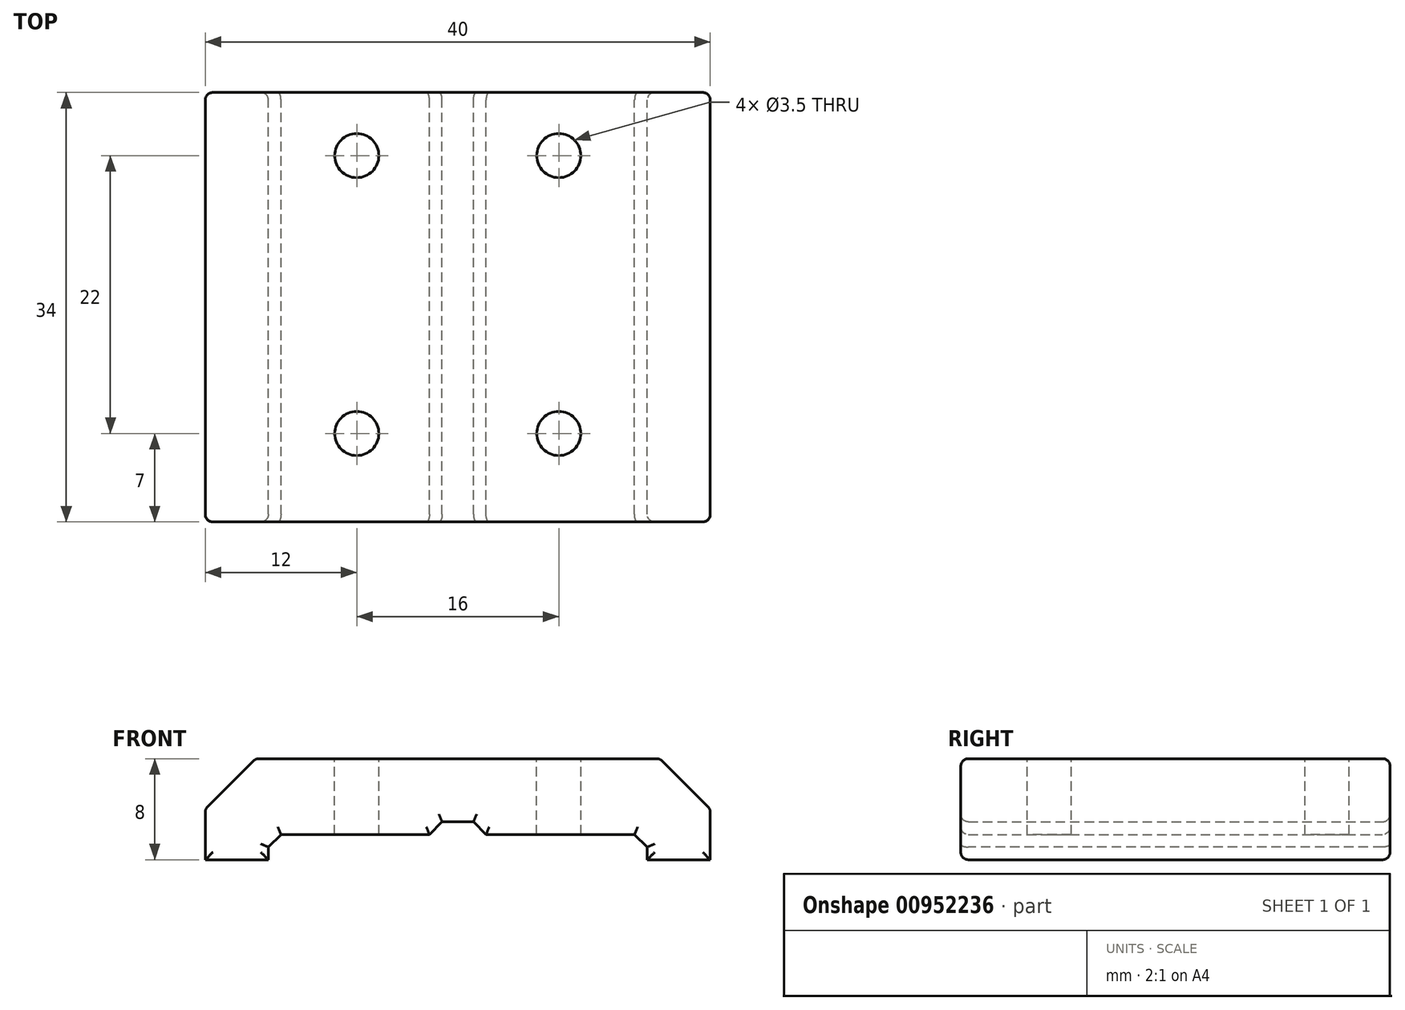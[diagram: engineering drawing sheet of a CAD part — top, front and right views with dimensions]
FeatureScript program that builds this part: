
annotation { "Feature Type Name" : "Feature", "Feature Type Description" : "" }
export const myFeature = defineFeature(function(context is Context, id is Id, definition is map)
    precondition{}
    {
        {
            var Q0;
            Q0=qCreatedBy(makeId("Front.planeOp"),FACE);
            var sketch = newSketch(context, id + "F0", { "sketchPlane" : qUnion([Q0])});
            skLineSegment(sketch, "E0", {"start": v(0, 0) * mm, "end": v(-20, 0) * mm});
            skLineSegment(sketch, "E1", {"start": v(-20, 0) * mm, "end": v(-20, -8) * mm});
            skLineSegment(sketch, "E2", {"start": v(-20, -8) * mm, "end": v(-15, -8) * mm});
            skLineSegment(sketch, "E3", {"start": v(-15, -8) * mm, "end": v(-15, -6) * mm});
            skLineSegment(sketch, "E4", {"start": v(-15, -6) * mm, "end": v(-2.24, -6) * mm});
            skLineSegment(sketch, "E5", {"start": v(-2.24, -6) * mm, "end": v(-1.24, -5) * mm});
            skLineSegment(sketch, "E6", {"start": v(-1.24, -5) * mm, "end": v(0, -5) * mm});
            skLineSegment(sketch, "E7", {"start": v(0, -5) * mm, "end": v(0, 0) * mm});
            skSolve(sketch);
        }
        {
            var Q0;
            Q0 = qSketchRegion(id + "F0", true);
            extrude(context, id + "F1", {"entities" : qUnion([Q0]), "depth" : 34 * mm, "offsetDistance" : 25 * mm});
        }
        {
            var Q0;
            Q0=makeQuery(id+"F1.opExtrude","SWEPT_FACE",FACE,{"disambiguationData":[OSD([sQuery(id+"F0.wireOp",EDGE,"E0")])]});
            var sketch = newSketch(context, id + "F2", { "sketchPlane" : qUnion([Q0])});
            skCircle(sketch, "E8", {"center": v(-8, -5) * mm, "radius": 1.75 * mm});
            skCircle(sketch, "E9", {"center": v(-8, -27) * mm, "radius": 1.75 * mm});
            skSolve(sketch);
        }
        {
            var Q0;
            Q0 = qSketchRegion(id + "F2", true);
            extrude(context, id + "F3", {"entities" : qUnion([Q0]), "operationType" : NewBodyOperationType.REMOVE, "endBound" : BoundingType.THROUGH_ALL, "oppositeDirection" : true, "depth" : 25 * mm, "offsetDistance" : 25 * mm});
        }
        {
            var Q0;
            Q0=makeQuery(id+"F1.opExtrude","SWEPT_EDGE",EDGE,{"disambiguationData":[OSD([sQuery(id+"F0.wireOp",EDGE,"E0"),sQuery(id+"F0.wireOp",EDGE,"E1")])]});
            chamfer(context, id + "F4", {"entities" : qUnion([Q0]), "width" : 4 * mm, "tangentPropagation" : true});
        }
        {
            var Q0;
            Q0=makeQuery(id+"F1.opExtrude","SWEPT_EDGE",EDGE,{"disambiguationData":[OSD([sQuery(id+"F0.wireOp",EDGE,"E3"),sQuery(id+"F0.wireOp",EDGE,"E4")])]});
            chamfer(context, id + "F5", {"entities" : qUnion([Q0]), "width" : 1 * mm, "tangentPropagation" : true});
        }
        {
            var Q0;
            Q0=makeQuery(id+"F1.opExtrude","SWEPT_BODY",BODY,{"disambiguationData":[OSD([sQuery(id+"F0.wireOp",EDGE,"E0"),sQuery(id+"F0.wireOp",EDGE,"E1"),sQuery(id+"F0.wireOp",EDGE,"E2"),sQuery(id+"F0.wireOp",EDGE,"E3"),sQuery(id+"F0.wireOp",EDGE,"E4"),sQuery(id+"F0.wireOp",EDGE,"E5"),sQuery(id+"F0.wireOp",EDGE,"E6"),sQuery(id+"F0.wireOp",EDGE,"E7")])]});
            var Q1;
            Q1=makeQuery(id+"F1.opExtrude","SWEPT_FACE",FACE,{"disambiguationData":[OSD([sQuery(id+"F0.wireOp",EDGE,"E7")])]});
            mirror(context, id + "F6", {"operationType" : NewBodyOperationType.ADD, "entities" : qUnion([Q0]), "mirrorPlane" : qUnion([Q1])});
        }
        {
            var Q0;
            {var subQ0=makeQuery(id+"F1.opExtrude","CAP_FACE",FACE,{"disambiguationData":[OSD([sQuery(id+"F0.wireOp",EDGE,"E0"),sQuery(id+"F0.wireOp",EDGE,"E1"),sQuery(id+"F0.wireOp",EDGE,"E2"),sQuery(id+"F0.wireOp",EDGE,"E3"),sQuery(id+"F0.wireOp",EDGE,"E4"),sQuery(id+"F0.wireOp",EDGE,"E5"),sQuery(id+"F0.wireOp",EDGE,"E6"),sQuery(id+"F0.wireOp",EDGE,"E7")])],"isStart":true});Q0=makeQuery(id+"F6.boolean.opBoolean","MERGE",FACE,{"derivedFrom":[subQ0,makeQuery(id+"F6.opPattern","COPY",FACE,{"derivedFrom":subQ0,"instanceName":"1"})]});}
            var sketch = newSketch(context, id + "F7", { "sketchPlane" : qUnion([Q0])});
            skArc(sketch, "E10", {"start": v(4.15, 0) * mm, "mid": v(0, 1.5) * mm, "end": v(-4.15, 0) * mm});
            skLineSegment(sketch, "E11", {"start": v(-4.15, 0) * mm, "end": v(4.15, 0) * mm});
            skSolve(sketch);
        }
        {
            var Q0;
            {var subQ0=makeQuery(id+"F1.opExtrude","CAP_FACE",FACE,{"disambiguationData":[OSD([sQuery(id+"F0.wireOp",EDGE,"E0"),sQuery(id+"F0.wireOp",EDGE,"E1"),sQuery(id+"F0.wireOp",EDGE,"E2"),sQuery(id+"F0.wireOp",EDGE,"E3"),sQuery(id+"F0.wireOp",EDGE,"E4"),sQuery(id+"F0.wireOp",EDGE,"E5"),sQuery(id+"F0.wireOp",EDGE,"E6"),sQuery(id+"F0.wireOp",EDGE,"E7")])],"isStart":true});Q0=makeQuery(id+"Ffjy7sloizKUaoE_1.boolean.opBoolean","MERGE",FACE,{"derivedFrom":[makeQuery(id+"F6.boolean.opBoolean","MERGE",FACE,{"derivedFrom":[subQ0,makeQuery(id+"F6.opPattern","COPY",FACE,{"derivedFrom":subQ0,"instanceName":"1"})]}),makeQuery(id+"Ffjy7sloizKUaoE_1.opExtrude","CAP_FACE",FACE,{"disambiguationData":[OSD([sQuery(id+"F7.wireOp",EDGE,"E10"),sQuery(id+"F7.wireOp",EDGE,"E11")])],"isStart":true})]});}
            var Q1;
            {var subQ0=makeQuery(id+"F1.opExtrude","CAP_FACE",FACE,{"disambiguationData":[OSD([sQuery(id+"F0.wireOp",EDGE,"E0"),sQuery(id+"F0.wireOp",EDGE,"E1"),sQuery(id+"F0.wireOp",EDGE,"E2"),sQuery(id+"F0.wireOp",EDGE,"E3"),sQuery(id+"F0.wireOp",EDGE,"E4"),sQuery(id+"F0.wireOp",EDGE,"E5"),sQuery(id+"F0.wireOp",EDGE,"E6"),sQuery(id+"F0.wireOp",EDGE,"E7")])],"isStart":false});Q1=makeQuery(id+"Ffjy7sloizKUaoE_1.boolean.opBoolean","MERGE",FACE,{"derivedFrom":[makeQuery(id+"F6.boolean.opBoolean","MERGE",FACE,{"derivedFrom":[subQ0,makeQuery(id+"F6.opPattern","COPY",FACE,{"derivedFrom":subQ0,"instanceName":"1"})]}),makeQuery(id+"Ffjy7sloizKUaoE_1.opExtrude","CAP_FACE",FACE,{"disambiguationData":[OSD([sQuery(id+"F7.wireOp",EDGE,"E10"),sQuery(id+"F7.wireOp",EDGE,"E11")])],"isStart":false})]});}
            var Q2;
            {var subQ0=sQuery(id+"F0.wireOp",EDGE,"E1");Q2=makeQuery(id+"F6.opPattern","COPY",EDGE,{"derivedFrom":makeQuery(id+"F4.opChamfer","BLEND_EDGE",EDGE,{"blendedFrom":[makeQuery(id+"F1.opExtrude","SWEPT_EDGE",EDGE,{"disambiguationData":[OSD([sQuery(id+"F0.wireOp",EDGE,"E0"),subQ0])]}),makeQuery(id+"F1.opExtrude","SWEPT_FACE",FACE,{"disambiguationData":[OSD([subQ0])]})],"blendedInto":[makeQuery(id+"F1.opExtrude","SWEPT_FACE",FACE,{"disambiguationData":[OSD([subQ0])]})]}),"instanceName":"1"});}
            var Q3;
            {var subQ0=sQuery(id+"F0.wireOp",EDGE,"E0");Q3=makeQuery(id+"F6.opPattern","COPY",EDGE,{"derivedFrom":makeQuery(id+"F4.opChamfer","BLEND_EDGE",EDGE,{"blendedFrom":[makeQuery(id+"F1.opExtrude","SWEPT_EDGE",EDGE,{"disambiguationData":[OSD([subQ0,sQuery(id+"F0.wireOp",EDGE,"E1")])]}),makeQuery(id+"F1.opExtrude","SWEPT_FACE",FACE,{"disambiguationData":[OSD([subQ0])]})],"blendedInto":[makeQuery(id+"F1.opExtrude","SWEPT_FACE",FACE,{"disambiguationData":[OSD([subQ0])]})]}),"instanceName":"1"});}
            var Q4;
            Q4=makeQuery(id+"F4.opChamfer","BLEND_FACE",FACE,{"disambiguationData":[OSD([sQuery(id+"F0.wireOp",EDGE,"E0"),sQuery(id+"F0.wireOp",EDGE,"E1")])]});
            fillet(context, id + "F8", {"entities" : qUnion([Q0, Q1, Q2, Q3, Q4]), "radius" : .6 * mm, "tangentPropagation" : true, "allowEdgeOverflow" : false});
        }
    });
